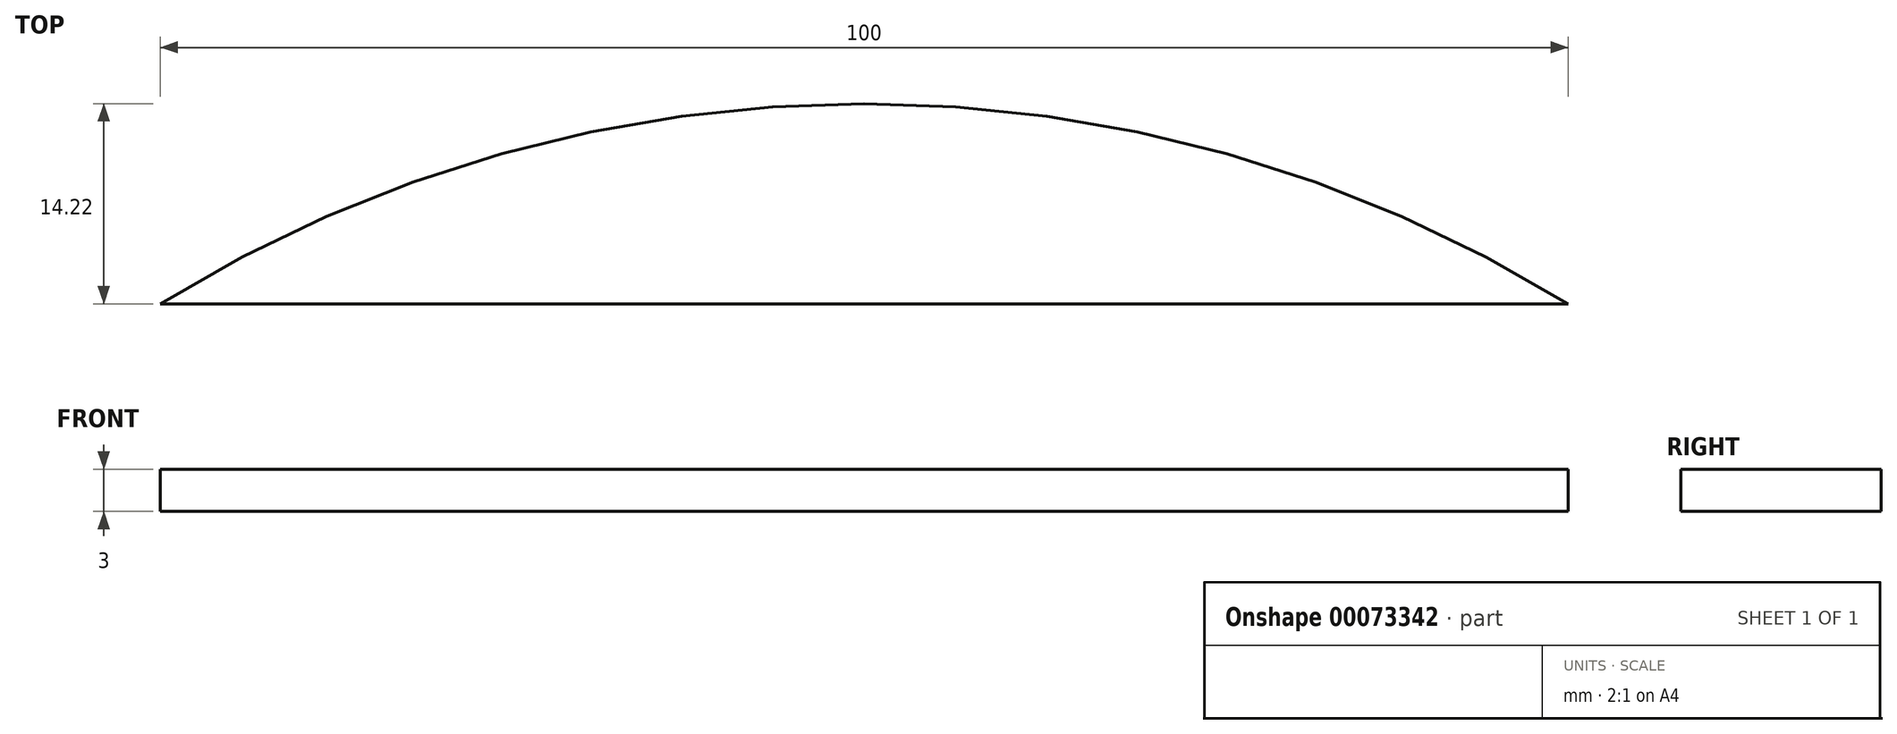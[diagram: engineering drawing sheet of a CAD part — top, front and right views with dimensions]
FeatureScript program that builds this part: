
annotation { "Feature Type Name" : "Feature", "Feature Type Description" : "" }
export const myFeature = defineFeature(function(context is Context, id is Id, definition is map)
    precondition{}
    {
        {
            var Q0;
            Q0=qCreatedBy(makeId("Top.planeOp"),FACE);
            var sketch = newSketch(context, id + "F0", { "sketchPlane" : qUnion([Q0])});
            skCircle(sketch, "E0", {"center": v(-25, 0) * mm, "radius": 95 * mm});
            skCircle(sketch, "E1", {"center": v(25, 0) * mm, "radius": 95 * mm});
            skLineSegment(sketch, "E2", {"start": v(-25, 0) * mm, "end": v(25, 0) * mm});
            skLineSegment(sketch, "E3", {"start": v(-75, 80.78) * mm, "end": v(75, 80.78) * mm});
            skLineSegment(sketch, "E4", {"start": v(-75, -80.78) * mm, "end": v(75, -80.78) * mm});
            skPoint(sketch, "E5", {"position": v(0, 0) * mm});
            skSolve(sketch);
        }
        {
            var Q0;
            {var subQ0=sQuery(id+"F0.wireOp",EDGE,"E3");var subQ1=sQuery(id+"F0.wireOp",EDGE,"E0");var subQ2=makeQuery(id+"F0.imprint","INTERSECT",VERTEX,{"disambiguationData":[OD(0.0)],"derivedFrom":[subQ1,subQ0]});Q0=makeQuery(id+"F0.imprint","IMPRINT",FACE,{"disambiguationData":[TD([[makeQuery(id+"F0.imprint","IMPRINT",EDGE,{"disambiguationData":[TD([[subQ2,-1.0]])],"derivedFrom":subQ1}),1.0]])]});}
            var Q1;
            {var subQ0=sQuery(id+"F0.wireOp",EDGE,"E3");var subQ1=sQuery(id+"F0.wireOp",EDGE,"E0");var subQ2=makeQuery(id+"F0.imprint","INTERSECT",VERTEX,{"disambiguationData":[OD(1.0)],"derivedFrom":[subQ1,subQ0]});Q1=makeQuery(id+"F0.imprint","IMPRINT",FACE,{"disambiguationData":[TD([[makeQuery(id+"F0.imprint","IMPRINT",EDGE,{"disambiguationData":[TD([[subQ2,1.0]])],"derivedFrom":subQ1}),1.0]])]});}
            var Q2;
            {var subQ0=sQuery(id+"F0.wireOp",EDGE,"E3");var subQ1=sQuery(id+"F0.wireOp",EDGE,"E0");var subQ2=makeQuery(id+"F0.imprint","INTERSECT",VERTEX,{"disambiguationData":[OD(1.0)],"derivedFrom":[subQ1,subQ0]});Q2=makeQuery(id+"F0.imprint","IMPRINT",FACE,{"disambiguationData":[TD([[makeQuery(id+"F0.imprint","IMPRINT",EDGE,{"disambiguationData":[TD([[subQ2,1.0]])],"derivedFrom":subQ1}),-1.0]])]});}
            extrude(context, id + "F1", {"entities" : qUnion([Q0, Q1, Q2]), "depth" : 3 * mm});
        }
        {
            var Q0;
            Q0=makeQuery(id+"F1.opExtrude","CAP_FACE",FACE,{"disambiguationData":[OSD([sQuery(id+"F0.wireOp",EDGE,"E0"),sQuery(id+"F0.wireOp",EDGE,"E1"),sQuery(id+"F0.wireOp",EDGE,"E3"),sQuery(id+"F0.wireOp",EDGE,"E4")])],"isStart":false});
            var sketch = newSketch(context, id + "F2", { "sketchPlane" : qUnion([Q0])});
            skLineSegment(sketch, "E6.bottom", {"start": v(-50, 50) * mm, "end": v(50, 50) * mm});
            skLineSegment(sketch, "E6.top", {"start": v(-50, -50) * mm, "end": v(50, -50) * mm});
            skLineSegment(sketch, "E6.left", {"start": v(-50, 50) * mm, "end": v(-50, -50) * mm});
            skLineSegment(sketch, "E6.right", {"start": v(50, 50) * mm, "end": v(50, -50) * mm});
            skLineSegment(sketch, "E7", {"start": v(-50, 50) * mm, "end": v(50, -50) * mm});
            skPoint(sketch, "E8", {"position": v(0, 0) * mm});
            skSolve(sketch);
        }
        {
            var Q0;
            Q0=sQuery(id+"F2.wireOp",VERTEX,"E6.left.start");
            var Q1;
            Q1=sQuery(id+"F2.wireOp",VERTEX,"E6.right.start");
            var Q2;
            Q2=sQuery(id+"F2.wireOp",VERTEX,"E6.top.end");
            var Q3;
            Q3=sQuery(id+"F2.wireOp",VERTEX,"E6.left.end");
            var Q4;
            Q4=makeQuery(id+"F1.opExtrude","SWEPT_BODY",BODY,{"disambiguationData":[OSD([sQuery(id+"F0.wireOp",EDGE,"E0"),sQuery(id+"F0.wireOp",EDGE,"E1"),sQuery(id+"F0.wireOp",EDGE,"E3"),sQuery(id+"F0.wireOp",EDGE,"E4")])]});
            hole(context, id + "F3", {"style" : HoleStyle.SIMPLE, "holeDiameter" : 3 * mm, "endStyle" : HoleEndStyle.THROUGH, "locations" : qUnion([Q0, Q1, Q2, Q3]), "scope" : qUnion([Q4])});
        }
        {
            var Q0;
            Q0=makeQuery(id+"F1.opExtrude","CAP_FACE",FACE,{"disambiguationData":[OSD([sQuery(id+"F0.wireOp",EDGE,"E0"),sQuery(id+"F0.wireOp",EDGE,"E1"),sQuery(id+"F0.wireOp",EDGE,"E3"),sQuery(id+"F0.wireOp",EDGE,"E4")])],"isStart":false});
            var sketch = newSketch(context, id + "F4", { "sketchPlane" : qUnion([Q0])});
            skCircle(sketch, "E9", {"center": v(0, 0) * mm, "radius": 40 * mm});
            skCircle(sketch, "E10", {"center": v(0, 0) * mm, "radius": 30 * mm});
            skLineSegment(sketch, "E11.bottom", {"start": v(-21.21, 21.21) * mm, "end": v(21.21, 21.21) * mm});
            skLineSegment(sketch, "E11.top", {"start": v(-21.21, -21.21) * mm, "end": v(21.21, -21.21) * mm});
            skLineSegment(sketch, "E11.left", {"start": v(-21.21, 21.21) * mm, "end": v(-21.21, -21.21) * mm});
            skLineSegment(sketch, "E11.right", {"start": v(21.21, 21.21) * mm, "end": v(21.21, -21.21) * mm});
            skSolve(sketch);
        }
        {
            var Q0;
            Q0=sQuery(id+"F4.wireOp",VERTEX,"E11.bottom.start");
            var Q1;
            Q1=sQuery(id+"F4.wireOp",VERTEX,"E11.right.start");
            var Q2;
            Q2=sQuery(id+"F4.wireOp",VERTEX,"E11.top.end");
            var Q3;
            Q3=sQuery(id+"F4.wireOp",VERTEX,"E11.left.end");
            var Q4;
            Q4=makeQuery(id+"F1.opExtrude","SWEPT_BODY",BODY,{"disambiguationData":[OSD([sQuery(id+"F0.wireOp",EDGE,"E0"),sQuery(id+"F0.wireOp",EDGE,"E1"),sQuery(id+"F0.wireOp",EDGE,"E3"),sQuery(id+"F0.wireOp",EDGE,"E4")])]});
            hole(context, id + "F5", {"style" : HoleStyle.SIMPLE, "holeDiameter" : 3 * mm, "endStyle" : HoleEndStyle.THROUGH, "locations" : qUnion([Q0, Q1, Q2, Q3]), "scope" : qUnion([Q4])});
        }
        {
            var Q0;
            Q0=makeQuery(id+"F1.opExtrude","CAP_FACE",FACE,{"disambiguationData":[OSD([sQuery(id+"F0.wireOp",EDGE,"E0"),sQuery(id+"F0.wireOp",EDGE,"E1"),sQuery(id+"F0.wireOp",EDGE,"E3"),sQuery(id+"F0.wireOp",EDGE,"E4")])],"isStart":true});
            var sketch = newSketch(context, id + "F6", { "sketchPlane" : qUnion([Q0])});
            skLineSegment(sketch, "E12.bottom", {"start": v(-28, 45) * mm, "end": v(28, 45) * mm});
            skLineSegment(sketch, "E12.top", {"start": v(-28, -40) * mm, "end": v(28, -40) * mm});
            skLineSegment(sketch, "E12.left", {"start": v(-28, 45) * mm, "end": v(-28, -40) * mm});
            skLineSegment(sketch, "E12.right", {"start": v(28, 45) * mm, "end": v(28, -40) * mm});
            skPoint(sketch, "E13", {"position": v(0, 0) * mm});
            skLineSegment(sketch, "E14.bottom", {"start": v(24.5, 41.5) * mm, "end": v(-24.5, 41.5) * mm});
            skLineSegment(sketch, "E14.top", {"start": v(24.5, -16.5) * mm, "end": v(-24.5, -16.5) * mm});
            skLineSegment(sketch, "E14.left", {"start": v(24.5, 41.5) * mm, "end": v(24.5, -16.5) * mm});
            skLineSegment(sketch, "E14.right", {"start": v(-24.5, 41.5) * mm, "end": v(-24.5, -16.5) * mm});
            skPoint(sketch, "E15", {"position": v(0, 41.5) * mm});
            skLineSegment(sketch, "E16", {"start": v(0, 0) * mm, "end": v(0, 41.5) * mm});
            skLineSegment(sketch, "E17", {"start": v(0, 0) * mm, "end": v(0, 45) * mm});
            skSolve(sketch);
        }
        {
            var Q0;
            Q0=sQuery(id+"F6.wireOp",VERTEX,"E14.right.start");
            var Q1;
            Q1=sQuery(id+"F6.wireOp",VERTEX,"E14.bottom.start");
            var Q2;
            Q2=sQuery(id+"F6.wireOp",VERTEX,"E14.left.end");
            var Q3;
            Q3=sQuery(id+"F6.wireOp",VERTEX,"E14.right.end");
            var Q4;
            Q4=makeQuery(id+"F1.opExtrude","SWEPT_BODY",BODY,{"disambiguationData":[OSD([sQuery(id+"F0.wireOp",EDGE,"E0"),sQuery(id+"F0.wireOp",EDGE,"E1"),sQuery(id+"F0.wireOp",EDGE,"E3"),sQuery(id+"F0.wireOp",EDGE,"E4")])]});
            hole(context, id + "F7", {"style" : HoleStyle.SIMPLE, "holeDiameter" : 3 * mm, "endStyle" : HoleEndStyle.THROUGH, "locations" : qUnion([Q0, Q1, Q2, Q3]), "scope" : qUnion([Q4])});
        }
        {
            var Q0;
            Q0=makeQuery(id+"F1.opExtrude","CAP_FACE",FACE,{"disambiguationData":[OSD([sQuery(id+"F0.wireOp",EDGE,"E0"),sQuery(id+"F0.wireOp",EDGE,"E1"),sQuery(id+"F0.wireOp",EDGE,"E3"),sQuery(id+"F0.wireOp",EDGE,"E4")])],"isStart":false});
            var sketch = newSketch(context, id + "F8", { "sketchPlane" : qUnion([Q0])});
            skLineSegment(sketch, "E18", {"start": v(0, 0) * mm, "end": v(-80, 0) * mm});
            skSolve(sketch);
        }
        {
            var Q0;
            Q0=sQuery(id+"F8.wireOp",VERTEX,"E18.end");
            var Q1;
            Q1=makeQuery(id+"F1.opExtrude","SWEPT_BODY",BODY,{"disambiguationData":[OSD([sQuery(id+"F0.wireOp",EDGE,"E0"),sQuery(id+"F0.wireOp",EDGE,"E1"),sQuery(id+"F0.wireOp",EDGE,"E3"),sQuery(id+"F0.wireOp",EDGE,"E4")])]});
            hole(context, id + "F9", {"style" : HoleStyle.SIMPLE, "holeDiameter" : 15 * mm, "endStyle" : HoleEndStyle.THROUGH, "locations" : qUnion([Q0]), "scope" : qUnion([Q1])});
        }
    });
